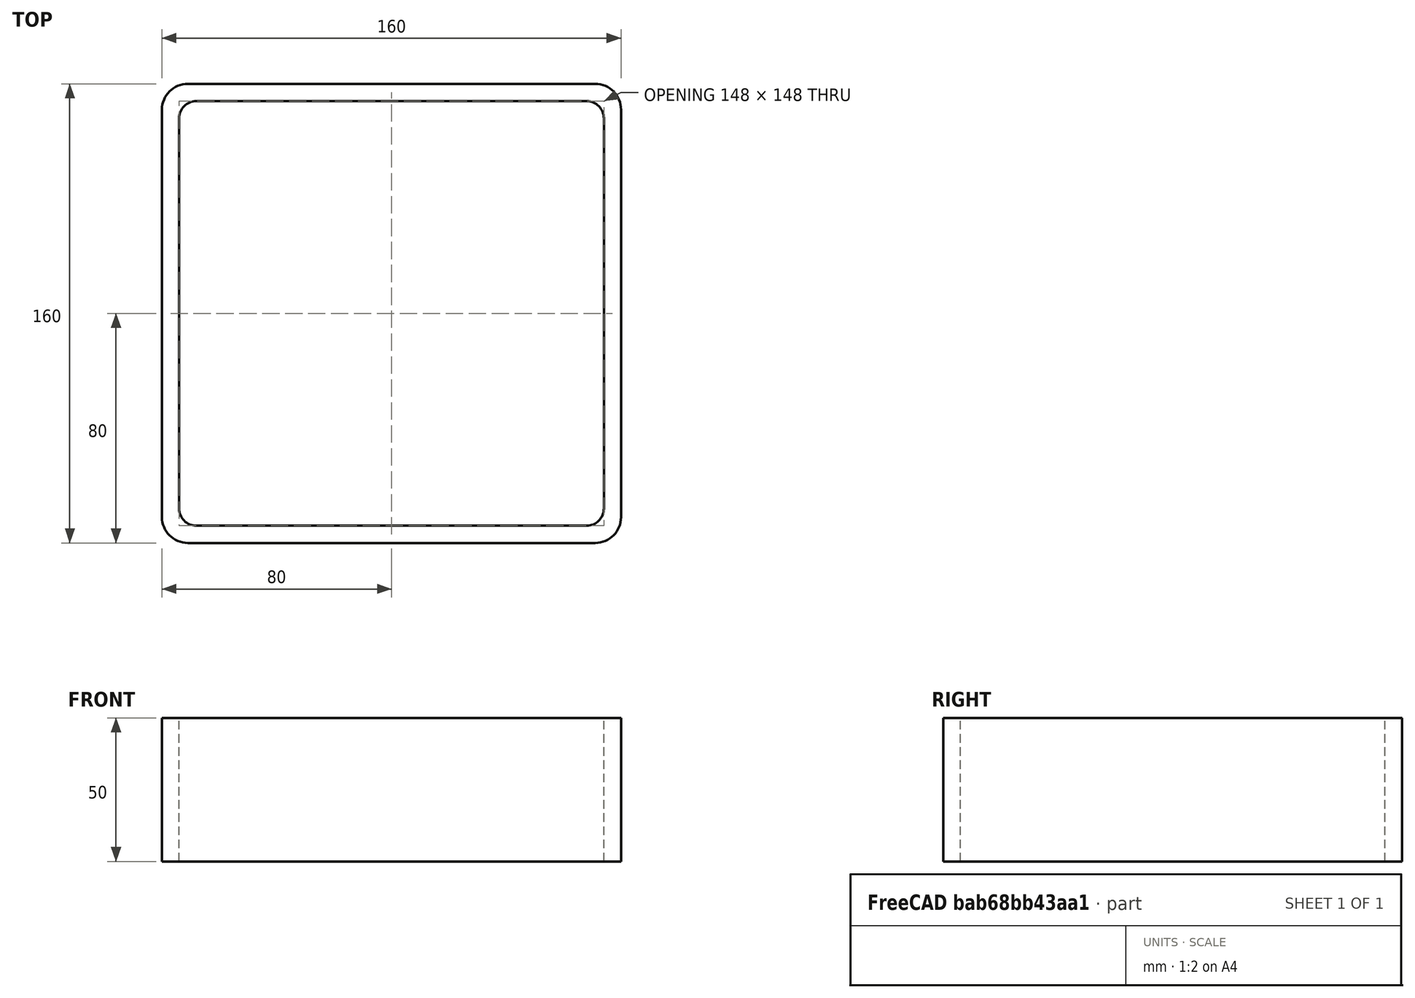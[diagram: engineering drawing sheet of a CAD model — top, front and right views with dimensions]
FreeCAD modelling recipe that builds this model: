
FCSTD DOCUMENT  (FreeCAD 0.15R4671 (Git))
Label: Square hollow section 160x160x6 EN10219 S235JRH
License: All rights reserved
LicenseURL: http://en.wikipedia.org/wiki/All_rights_reserved
objects: Sketcher::SketchObject×1, Part::Extrusion×1
note: 2 computed .brp shape members not serialized (recipe doc carries the construction recipe); baked Part::Feature solids carry a one-line shape summary decoded from their .brp

FEATURE [Sketcher::SketchObject] Sketch
  sketch-geometry (16):
    g0: LineSegment StartX=-68 StartY=74 StartZ=0 EndX=68 EndY=74 EndZ=0
    g1: LineSegment StartX=74 StartY=68 StartZ=0 EndX=74 EndY=-68 EndZ=0
    g2: LineSegment StartX=68 StartY=-74 StartZ=0 EndX=-68 EndY=-74 EndZ=0
    g3: LineSegment StartX=-74 StartY=-68 StartZ=0 EndX=-74 EndY=68 EndZ=0
    g4: LineSegment StartX=-71 StartY=80 StartZ=0 EndX=71 EndY=80 EndZ=0
    g5: LineSegment StartX=80 StartY=71 StartZ=0 EndX=80 EndY=-71 EndZ=0
    g6: LineSegment StartX=71 StartY=-80 StartZ=0 EndX=-71 EndY=-80 EndZ=0
    g7: LineSegment StartX=-80 StartY=-71 StartZ=0 EndX=-80 EndY=71 EndZ=0
    g8: ArcOfCircle CenterX=-68 CenterY=68 CenterZ=0 NormalX=0 NormalY=0 NormalZ=1 Radius=6 StartAngle=1.5708 EndAngle=3.14159
    g9: ArcOfCircle CenterX=68 CenterY=68 CenterZ=0 NormalX=0 NormalY=0 NormalZ=1 Radius=6 StartAngle=0 EndAngle=1.5708
    g10: ArcOfCircle CenterX=68 CenterY=-68 CenterZ=0 NormalX=0 NormalY=0 NormalZ=1 Radius=6 StartAngle=4.71239 EndAngle=6.28319
    g11: ArcOfCircle CenterX=-68 CenterY=-68 CenterZ=0 NormalX=0 NormalY=0 NormalZ=1 Radius=6 StartAngle=3.14159 EndAngle=4.71239
    g12: ArcOfCircle CenterX=71 CenterY=71 CenterZ=0 NormalX=0 NormalY=0 NormalZ=1 Radius=9 StartAngle=0 EndAngle=1.5708
    g13: ArcOfCircle CenterX=71 CenterY=-71 CenterZ=0 NormalX=0 NormalY=0 NormalZ=1 Radius=9 StartAngle=4.71239 EndAngle=6.28319
    g14: ArcOfCircle CenterX=-71 CenterY=-71 CenterZ=0 NormalX=0 NormalY=0 NormalZ=1 Radius=9 StartAngle=3.14159 EndAngle=4.71239
    g15: ArcOfCircle CenterX=-71 CenterY=71 CenterZ=0 NormalX=0 NormalY=0 NormalZ=1 Radius=9 StartAngle=1.5708 EndAngle=3.14159
  constraints (36):
    c: Horizontal(g2)
    c: Vertical(g3)
    c: Horizontal(g6)
    c: Vertical(g7)
    c: Tangent(g3,g8) = 1.5708
    c: Tangent(g0,g8) = 1.5708
    c: Tangent(g0,g9) = 1.5708
    c: Tangent(g1,g9) = 1.5708
    c: Tangent(g1,g10) = 1.5708
    c: Tangent(g2,g10) = 1.5708
    c: Tangent(g2,g11) = 1.5708
    c: Tangent(g3,g11) = 1.5708
    c: Tangent(g4,g12) = 1.5708
    c: Tangent(g5,g12) = 1.5708
    c: Tangent(g5,g13) = 1.5708
    c: Tangent(g6,g13) = 1.5708
    c: Tangent(g6,g14) = 1.5708
    c: Tangent(g7,g14) = 1.5708
    c: Tangent(g7,g15) = 1.5708
    c: Tangent(g4,g15) = 1.5708
    c: Equal(g9,g8)
    c: Equal(g9,g11)
    c: Equal(g9,g10)
    c: Equal(g12,g15)
    c: Equal(g12,g14)
    c: Equal(g12,g13)
    c: Symmetric(g4,g6,g-1)
    c: Symmetric(g7,g5,g-2)
    c: DistanceY(g4,g6) = -160
    c: DistanceX(g7,g5) = 160
    c: Symmetric(g3,g1,g-2)
    c: Symmetric(g0,g2,g-1)
    c: DistanceY(g0,g4) = 6
    c: DistanceX(g5,g1) = -6
    c: Radius(g9) = 6
    c: Radius(g12) = 9
FEATURE [Part::Extrusion] Extrude  label="Square hollow section 160x160x6 EN10219 S235JRH"
  Base = -> Sketch
  Dir = (0,0,50)
  Solid = true
